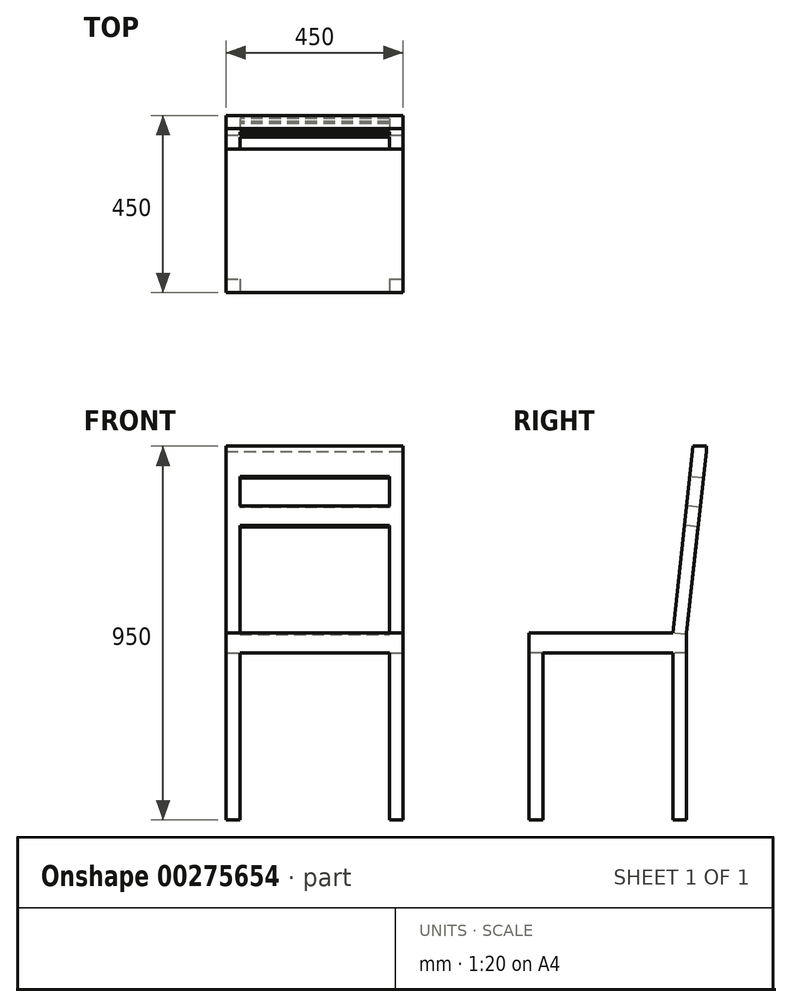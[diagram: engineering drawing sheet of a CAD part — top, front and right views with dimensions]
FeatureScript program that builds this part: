
annotation { "Feature Type Name" : "Feature", "Feature Type Description" : "" }
export const myFeature = defineFeature(function(context is Context, id is Id, definition is map)
    precondition{}
    {
        {
            var Q0;
            Q0=qCreatedBy(makeId("Top.planeOp"),FACE);
            var sketch = newSketch(context, id + "F0", { "sketchPlane" : qUnion([Q0])});
            skLineSegment(sketch, "E0.bottom", {"start": v(225, 225) * mm, "end": v(-225, 225) * mm});
            skLineSegment(sketch, "E0.top", {"start": v(225, -225) * mm, "end": v(-225, -225) * mm});
            skLineSegment(sketch, "E0.left", {"start": v(225, 225) * mm, "end": v(225, -225) * mm});
            skLineSegment(sketch, "E0.right", {"start": v(-225, 225) * mm, "end": v(-225, -225) * mm});
            skPoint(sketch, "E0.middle", {"position": v(0, 0) * mm});
            skSolve(sketch);
        }
        {
            var Q0;
            Q0=qSketchRegion(id+"F0",true);
            extrude(context, id + "F1", {"entities" : qUnion([Q0]), "depth" : 950 * mm});
        }
        {
            var Q0;
            Q0=makeQuery(id+"F1.opExtrude","SWEPT_FACE",FACE,{"disambiguationData":[OSD([sQuery(id+"F0.wireOp",EDGE,"E0.left")])]});
            var sketch = newSketch(context, id + "F2", { "sketchPlane" : qUnion([Q0])});
            skLineSegment(sketch, "E1.bottom", {"start": v(-225, 475) * mm, "end": v(225, 475) * mm});
            skLineSegment(sketch, "E1.top", {"start": v(-225, 425) * mm, "end": v(225, 425) * mm});
            skLineSegment(sketch, "E1.left", {"start": v(-225, 475) * mm, "end": v(-225, 425) * mm});
            skLineSegment(sketch, "E1.right", {"start": v(225, 475) * mm, "end": v(225, 425) * mm});
            skLineSegment(sketch, "E2", {"start": v(175, 475) * mm, "end": v(225, 935.7) * mm});
            skLineSegment(sketch, "E3", {"start": v(140, 475) * mm, "end": v(191.55, 950) * mm});
            skLineSegment(sketch, "E4", {"start": v(140, 475) * mm, "end": v(140, 0) * mm});
            skLineSegment(sketch, "E5", {"start": v(175, 475) * mm, "end": v(175, 0) * mm});
            skLineSegment(sketch, "E6", {"start": v(-190, 425) * mm, "end": v(-190, 0) * mm});
            skSolve(sketch);
        }
        {
            var Q0;
            {var subQ4=sQuery(id+"F2.wireOp",EDGE,"E3");Q0=makeQuery(id+"F2.imprint","IMPRINT",FACE,{"disambiguationData":[TD([[makeQuery(id+"F2.imprint","IMPRINT",EDGE,{"derivedFrom":subQ4}),1.0]])]});}
            var Q1;
            {var subQ3=sQuery(id+"F2.wireOp",EDGE,"E2");Q1=makeQuery(id+"F2.imprint","IMPRINT",FACE,{"disambiguationData":[TD([[makeQuery(id+"F2.imprint","IMPRINT",EDGE,{"derivedFrom":subQ3}),-1.0]])]});}
            var Q2;
            {var subQ0=sQuery(id+"F2.wireOp",EDGE,"E1.right");Q2=makeQuery(id+"F2.imprint","IMPRINT",FACE,{"disambiguationData":[TD([[makeQuery(id+"F2.imprint","IMPRINT",EDGE,{"derivedFrom":subQ0}),-1.0]])]});}
            var Q3;
            {var subQ1=sQuery(id+"F0.wireOp",EDGE,"E0.left");var subQ4=sQuery(id+"F2.wireOp",EDGE,"E5");var subQ6=makeQuery(id+"F1.opExtrude","CAP_EDGE",EDGE,{"disambiguationData":[OSD([subQ1])],"isStart":true});var subQ7=makeQuery(id+"F2.imprint","INTERSECT",VERTEX,{"derivedFrom":[subQ6,subQ4]});Q3=makeQuery(id+"F2.imprint","IMPRINT",FACE,{"disambiguationData":[TD([[makeQuery(id+"F2.imprint","IMPRINT",EDGE,{"disambiguationData":[TD([[subQ7,1.0]])],"derivedFrom":subQ4}),1.0]])]});}
            var Q4;
            {var subQ0=sQuery(id+"F2.wireOp",EDGE,"E6");Q4=makeQuery(id+"F2.imprint","IMPRINT",FACE,{"disambiguationData":[TD([[makeQuery(id+"F2.imprint","IMPRINT",EDGE,{"derivedFrom":subQ0}),1.0]])]});}
            extrude(context, id + "F3", {"entities" : qUnion([Q0, Q1, Q2, Q3, Q4]), "operationType" : NewBodyOperationType.REMOVE, "endBound" : BoundingType.THROUGH_ALL, "oppositeDirection" : true, "depth" : 25 * mm});
        }
        {
            var Q0;
            Q0=makeQuery(id+"F1.opExtrude","SWEPT_FACE",FACE,{"disambiguationData":[OSD([sQuery(id+"F0.wireOp",EDGE,"E0.top")])]});
            var sketch = newSketch(context, id + "F4", { "sketchPlane" : qUnion([Q0])});
            skLineSegment(sketch, "E7.bottom", {"start": v(-190, 0) * mm, "end": v(190, 0) * mm});
            skLineSegment(sketch, "E7.top", {"start": v(-190, 425) * mm, "end": v(190, 425) * mm});
            skLineSegment(sketch, "E7.left", {"start": v(-190, 0) * mm, "end": v(-190, 425) * mm});
            skLineSegment(sketch, "E7.right", {"start": v(190, 0) * mm, "end": v(190, 425) * mm});
            skSolve(sketch);
        }
        {
            var Q0;
            Q0=makeQuery(id+"F4.imprint","IMPRINT",FACE,{"disambiguationData":[TD([[makeQuery(id+"F4.imprint","IMPRINT",EDGE,{"derivedFrom":sQuery(id+"F4.wireOp",EDGE,"E7.bottom")}),-1.0]])]});
            extrude(context, id + "F5", {"entities" : qUnion([Q0]), "operationType" : NewBodyOperationType.REMOVE, "endBound" : BoundingType.THROUGH_ALL, "oppositeDirection" : true, "depth" : 25 * mm});
        }
        {
            var Q0;
            Q0=makeQuery(id+"F3.boolean.opBoolean","COPY",FACE,{"derivedFrom":makeQuery(id+"F3.opExtrude","SWEPT_FACE",FACE,{"disambiguationData":[OSD([sQuery(id+"F2.wireOp",EDGE,"E3")])]})});
            var sketch = newSketch(context, id + "F6", { "sketchPlane" : qUnion([Q0])});
            skLineSegment(sketch, "E8.bottom", {"start": v(-190, 487.33) * mm, "end": v(190, 487.33) * mm});
            skLineSegment(sketch, "E8.top", {"start": v(-190, 887.33) * mm, "end": v(190, 887.33) * mm});
            skLineSegment(sketch, "E8.left", {"start": v(-190, 487.33) * mm, "end": v(-190, 887.33) * mm});
            skLineSegment(sketch, "E8.right", {"start": v(190, 487.33) * mm, "end": v(190, 887.33) * mm});
            skLineSegment(sketch, "E9.bottom", {"start": v(-190, 812.33) * mm, "end": v(190, 812.33) * mm});
            skLineSegment(sketch, "E9.top", {"start": v(-190, 762.33) * mm, "end": v(190, 762.33) * mm});
            skLineSegment(sketch, "E9.left", {"start": v(-190, 812.33) * mm, "end": v(-190, 762.33) * mm});
            skLineSegment(sketch, "E9.right", {"start": v(190, 812.33) * mm, "end": v(190, 762.33) * mm});
            skSolve(sketch);
        }
        {
            var Q0;
            {var subQ0=sQuery(id+"F6.wireOp",EDGE,"E8.top");Q0=makeQuery(id+"F6.imprint","IMPRINT",FACE,{"disambiguationData":[TD([[makeQuery(id+"F6.imprint","IMPRINT",EDGE,{"derivedFrom":subQ0}),-1.0]])]});}
            var Q1;
            {var subQ0=sQuery(id+"F6.wireOp",EDGE,"E8.bottom");Q1=makeQuery(id+"F6.imprint","IMPRINT",FACE,{"disambiguationData":[TD([[makeQuery(id+"F6.imprint","IMPRINT",EDGE,{"derivedFrom":subQ0}),1.0]])]});}
            extrude(context, id + "F7", {"entities" : qUnion([Q0, Q1]), "operationType" : NewBodyOperationType.REMOVE, "endBound" : BoundingType.THROUGH_ALL, "oppositeDirection" : true, "depth" : 25 * mm});
        }
    });
